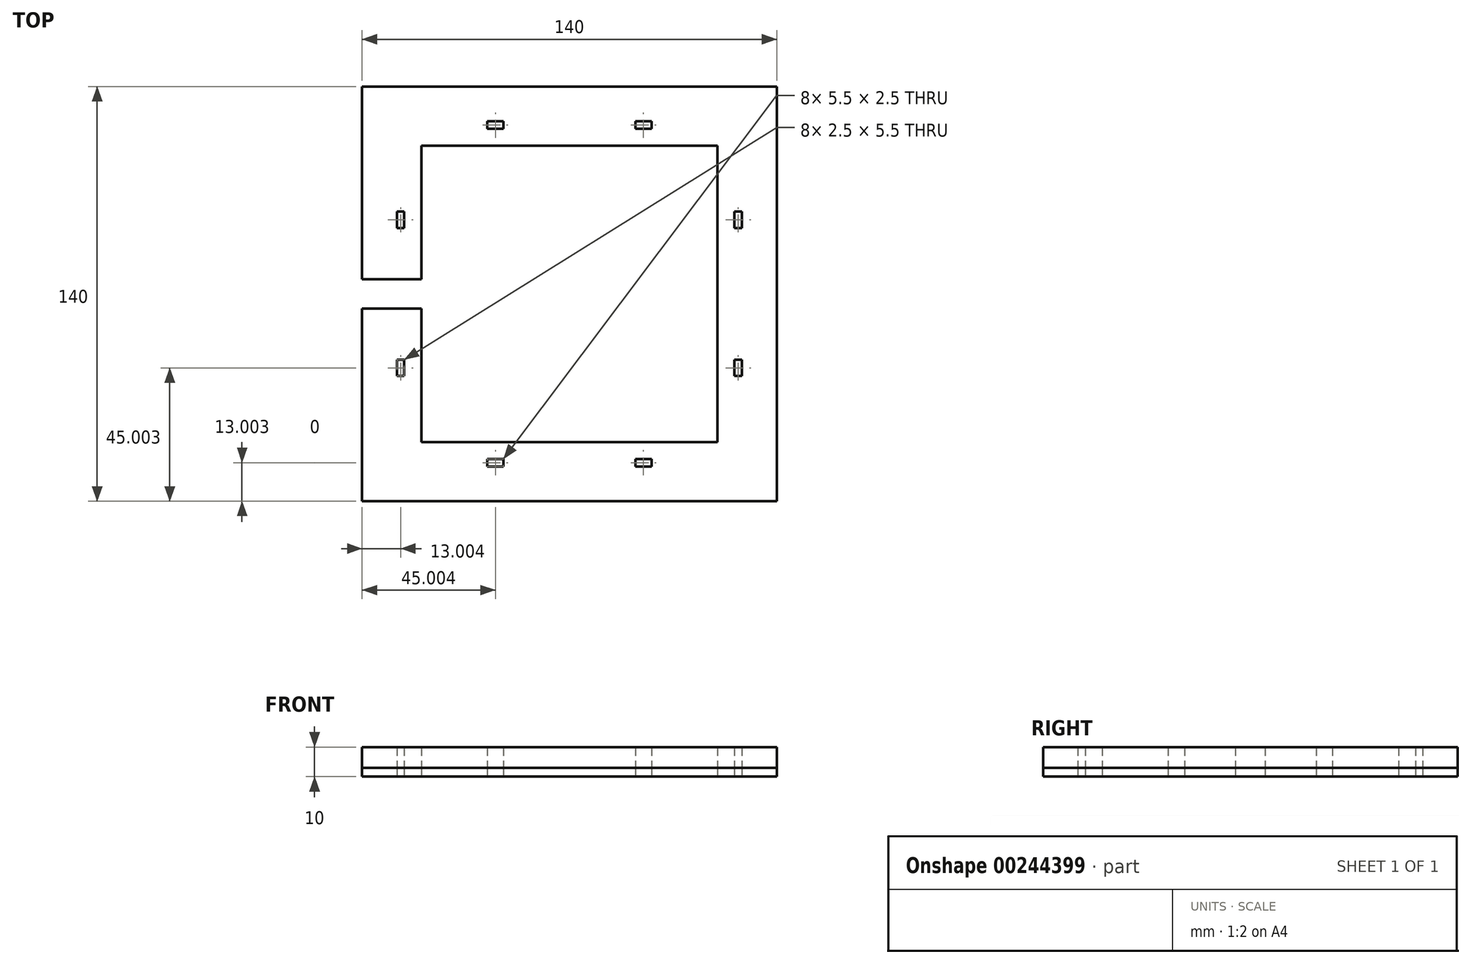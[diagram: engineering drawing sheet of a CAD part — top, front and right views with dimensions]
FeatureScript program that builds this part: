
annotation { "Feature Type Name" : "Feature", "Feature Type Description" : "" }
export const myFeature = defineFeature(function(context is Context, id is Id, definition is map)
    precondition{}
    {
        {
            var Q0;
            Q0=qCreatedBy(makeId("Top.planeOp"),FACE);
            var sketch = newSketch(context, id + "F0", { "sketchPlane" : qUnion([Q0])});
            skLineSegment(sketch, "E0.bottom", {"start": v(-61.18, 64.73) * mm, "end": v(38.82, 64.73) * mm});
            skLineSegment(sketch, "E0.top", {"start": v(-61.18, -35.27) * mm, "end": v(38.82, -35.27) * mm});
            skLineSegment(sketch, "E0.left", {"start": v(-61.18, 64.73) * mm, "end": v(-61.18, -35.27) * mm});
            skLineSegment(sketch, "E0.right", {"start": v(38.82, 64.73) * mm, "end": v(38.82, -35.27) * mm});
            skLineSegment(sketch, "E1.bottom", {"start": v(-81.18, 84.73) * mm, "end": v(58.82, 84.73) * mm});
            skLineSegment(sketch, "E1.top", {"start": v(-81.18, -55.27) * mm, "end": v(58.82, -55.27) * mm});
            skLineSegment(sketch, "E1.left", {"start": v(-81.18, 84.73) * mm, "end": v(-81.18, -55.27) * mm});
            skLineSegment(sketch, "E1.right", {"start": v(58.82, 84.73) * mm, "end": v(58.82, -55.27) * mm});
            skPoint(sketch, "E2", {"position": v(-11.18, 14.73) * mm});
            skLineSegment(sketch, "E3.bottom", {"start": v(53.82, -50.27) * mm, "end": v(-76.18, -50.27) * mm});
            skLineSegment(sketch, "E3.top", {"start": v(53.82, 79.73) * mm, "end": v(-76.18, 79.73) * mm});
            skLineSegment(sketch, "E3.left", {"start": v(53.82, -50.27) * mm, "end": v(53.82, 79.73) * mm});
            skLineSegment(sketch, "E3.right", {"start": v(-76.18, -50.27) * mm, "end": v(-76.18, 79.73) * mm});
            skLineSegment(sketch, "E4", {"start": v(-76.18, 71.73) * mm, "end": v(53.82, 71.73) * mm, "construction": true});
            skPoint(sketch, "E5", {"position": v(-36.18, 71.73) * mm});
            skPoint(sketch, "E6", {"position": v(13.82, 71.73) * mm});
            skLineSegment(sketch, "E7.bottom", {"start": v(-33.43, 70.48) * mm, "end": v(-38.93, 70.48) * mm});
            skLineSegment(sketch, "E7.top", {"start": v(-33.43, 72.98) * mm, "end": v(-38.93, 72.98) * mm});
            skLineSegment(sketch, "E7.left", {"start": v(-33.43, 70.48) * mm, "end": v(-33.43, 72.98) * mm});
            skLineSegment(sketch, "E7.right", {"start": v(-38.93, 70.48) * mm, "end": v(-38.93, 72.98) * mm});
            skPoint(sketch, "E8", {"position": v(-11.18, 71.73) * mm});
            skLineSegment(sketch, "E9", {"start": v(-11.18, 71.73) * mm, "end": v(-11.18, 68.28) * mm, "construction": true});
            skLineSegment(sketch, "E10.MirrorCS", {"start": v(11.07, 70.48) * mm, "end": v(11.07, 72.98) * mm});
            skLineSegment(sketch, "E11.MirrorCS", {"start": v(11.07, 72.98) * mm, "end": v(16.57, 72.98) * mm});
            skLineSegment(sketch, "E12.MirrorCS", {"start": v(16.57, 70.48) * mm, "end": v(16.57, 72.98) * mm});
            skLineSegment(sketch, "E13.MirrorCS", {"start": v(11.07, 70.48) * mm, "end": v(16.57, 70.48) * mm});
            skLineSegment(sketch, "E14.1.0", {"start": v(-69.43, -7.52) * mm, "end": v(-69.43, -13.02) * mm});
            skLineSegment(sketch, "E14.1.1", {"start": v(-66.93, -7.52) * mm, "end": v(-66.93, -13.02) * mm});
            skLineSegment(sketch, "E14.1.2", {"start": v(-66.93, -7.52) * mm, "end": v(-69.43, -7.52) * mm});
            skPoint(sketch, "E14.1.3", {"position": v(-68.18, -10.27) * mm});
            skLineSegment(sketch, "E14.1.4", {"start": v(-66.93, -13.02) * mm, "end": v(-69.43, -13.02) * mm});
            skPoint(sketch, "E14.1.5", {"position": v(-68.18, -10.27) * mm});
            skLineSegment(sketch, "E14.1.6", {"start": v(-69.43, 36.98) * mm, "end": v(-69.43, 42.48) * mm});
            skLineSegment(sketch, "E14.1.7", {"start": v(-66.93, 36.98) * mm, "end": v(-66.93, 42.48) * mm});
            skLineSegment(sketch, "E14.1.8", {"start": v(-66.93, 42.48) * mm, "end": v(-69.43, 42.48) * mm});
            skLineSegment(sketch, "E14.1.9", {"start": v(-66.93, 36.98) * mm, "end": v(-69.43, 36.98) * mm});
            skPoint(sketch, "E14.1.10", {"position": v(-68.18, 39.73) * mm});
            skLineSegment(sketch, "E14.1.11", {"start": v(-66.93, 36.98) * mm, "end": v(-66.93, 42.48) * mm});
            skLineSegment(sketch, "E14.1.12", {"start": v(-69.43, 36.98) * mm, "end": v(-69.43, 42.48) * mm});
            skLineSegment(sketch, "E14.1.13", {"start": v(-66.93, 36.98) * mm, "end": v(-69.43, 36.98) * mm});
            skLineSegment(sketch, "E14.1.14", {"start": v(-66.93, 42.48) * mm, "end": v(-69.43, 42.48) * mm});
            skPoint(sketch, "E14.1.15", {"position": v(-68.18, 39.73) * mm});
            skPoint(sketch, "E14.1.16", {"position": v(-68.18, 39.73) * mm});
            skPoint(sketch, "E14.1.17", {"position": v(-68.18, 39.73) * mm});
            skPoint(sketch, "E14.1.18", {"position": v(-68.18, 39.73) * mm});
            skLineSegment(sketch, "E14.2.0", {"start": v(11.07, -43.52) * mm, "end": v(16.57, -43.52) * mm});
            skLineSegment(sketch, "E14.2.1", {"start": v(11.07, -41.02) * mm, "end": v(16.57, -41.02) * mm});
            skLineSegment(sketch, "E14.2.2", {"start": v(11.07, -41.02) * mm, "end": v(11.07, -43.52) * mm});
            skPoint(sketch, "E14.2.3", {"position": v(13.82, -42.27) * mm});
            skLineSegment(sketch, "E14.2.4", {"start": v(16.57, -41.02) * mm, "end": v(16.57, -43.52) * mm});
            skPoint(sketch, "E14.2.5", {"position": v(13.82, -42.27) * mm});
            skLineSegment(sketch, "E14.2.6", {"start": v(-33.43, -43.52) * mm, "end": v(-38.93, -43.52) * mm});
            skLineSegment(sketch, "E14.2.7", {"start": v(-33.43, -41.02) * mm, "end": v(-38.93, -41.02) * mm});
            skLineSegment(sketch, "E14.2.8", {"start": v(-38.93, -41.02) * mm, "end": v(-38.93, -43.52) * mm});
            skLineSegment(sketch, "E14.2.9", {"start": v(-33.43, -41.02) * mm, "end": v(-33.43, -43.52) * mm});
            skPoint(sketch, "E14.2.10", {"position": v(-36.18, -42.27) * mm});
            skLineSegment(sketch, "E14.2.11", {"start": v(-33.43, -41.02) * mm, "end": v(-38.93, -41.02) * mm});
            skLineSegment(sketch, "E14.2.12", {"start": v(-33.43, -43.52) * mm, "end": v(-38.93, -43.52) * mm});
            skLineSegment(sketch, "E14.2.13", {"start": v(-33.43, -41.02) * mm, "end": v(-33.43, -43.52) * mm});
            skLineSegment(sketch, "E14.2.14", {"start": v(-38.93, -41.02) * mm, "end": v(-38.93, -43.52) * mm});
            skPoint(sketch, "E14.2.15", {"position": v(-36.18, -42.27) * mm});
            skPoint(sketch, "E14.2.16", {"position": v(-36.18, -42.27) * mm});
            skPoint(sketch, "E14.2.17", {"position": v(-36.18, -42.27) * mm});
            skPoint(sketch, "E14.2.18", {"position": v(-36.18, -42.27) * mm});
            skLineSegment(sketch, "E14.3.0", {"start": v(47.07, 36.98) * mm, "end": v(47.07, 42.48) * mm});
            skLineSegment(sketch, "E14.3.1", {"start": v(44.57, 36.98) * mm, "end": v(44.57, 42.48) * mm});
            skLineSegment(sketch, "E14.3.2", {"start": v(44.57, 36.98) * mm, "end": v(47.07, 36.98) * mm});
            skPoint(sketch, "E14.3.3", {"position": v(45.82, 39.73) * mm});
            skLineSegment(sketch, "E14.3.4", {"start": v(44.57, 42.48) * mm, "end": v(47.07, 42.48) * mm});
            skPoint(sketch, "E14.3.5", {"position": v(45.82, 39.73) * mm});
            skLineSegment(sketch, "E14.3.6", {"start": v(47.07, -7.52) * mm, "end": v(47.07, -13.02) * mm});
            skLineSegment(sketch, "E14.3.7", {"start": v(44.57, -7.52) * mm, "end": v(44.57, -13.02) * mm});
            skLineSegment(sketch, "E14.3.8", {"start": v(44.57, -13.02) * mm, "end": v(47.07, -13.02) * mm});
            skLineSegment(sketch, "E14.3.9", {"start": v(44.57, -7.52) * mm, "end": v(47.07, -7.52) * mm});
            skPoint(sketch, "E14.3.10", {"position": v(45.82, -10.27) * mm});
            skLineSegment(sketch, "E14.3.11", {"start": v(44.57, -7.52) * mm, "end": v(44.57, -13.02) * mm});
            skLineSegment(sketch, "E14.3.12", {"start": v(47.07, -7.52) * mm, "end": v(47.07, -13.02) * mm});
            skLineSegment(sketch, "E14.3.13", {"start": v(44.57, -7.52) * mm, "end": v(47.07, -7.52) * mm});
            skLineSegment(sketch, "E14.3.14", {"start": v(44.57, -13.02) * mm, "end": v(47.07, -13.02) * mm});
            skPoint(sketch, "E14.3.15", {"position": v(45.82, -10.27) * mm});
            skPoint(sketch, "E14.3.16", {"position": v(45.82, -10.27) * mm});
            skPoint(sketch, "E14.3.17", {"position": v(45.82, -10.27) * mm});
            skPoint(sketch, "E14.3.18", {"position": v(45.82, -10.27) * mm});
            skLineSegment(sketch, "E15", {"start": v(58.82, 14.73) * mm, "end": v(-81.18, 14.73) * mm, "construction": true});
            skLineSegment(sketch, "E16.bottom", {"start": v(-81.18, 19.73) * mm, "end": v(-61.18, 19.73) * mm});
            skLineSegment(sketch, "E16.top", {"start": v(-81.18, 9.73) * mm, "end": v(-61.18, 9.73) * mm});
            skLineSegment(sketch, "E16.left", {"start": v(-81.18, 19.73) * mm, "end": v(-81.18, 9.73) * mm});
            skLineSegment(sketch, "E16.right", {"start": v(-61.18, 19.73) * mm, "end": v(-61.18, 9.73) * mm});
            skLineSegment(sketch, "E17", {"start": v(-65.7, 14.73) * mm, "end": v(-65.7, 19.73) * mm, "construction": true});
            skLineSegment(sketch, "E18", {"start": v(-65.7, 19.73) * mm, "end": v(-65.7, 14.73) * mm, "construction": true});
            skLineSegment(sketch, "E19", {"start": v(-65.7, 9.73) * mm, "end": v(-65.7, 14.73) * mm, "construction": true});
            skSolve(sketch);
        }
        {
            var Q0;
            {var subQ5=sQuery(id+"F0.wireOp",EDGE,"E0.bottom");Q0=makeQuery(id+"F0.imprint","IMPRINT",FACE,{"disambiguationData":[TD([[makeQuery(id+"F0.imprint","IMPRINT",EDGE,{"derivedFrom":subQ5}),1.0]])]});}
            var Q1;
            {var subQ10=sQuery(id+"F0.wireOp",EDGE,"E1.bottom");Q1=makeQuery(id+"F0.imprint","IMPRINT",FACE,{"disambiguationData":[TD([[makeQuery(id+"F0.imprint","IMPRINT",EDGE,{"derivedFrom":subQ10}),-1.0]])]});}
            var Q2;
            {var subQ5=sQuery(id+"F0.wireOp",EDGE,"E16.right");Q2=makeQuery(id+"F0.imprint","IMPRINT",FACE,{"disambiguationData":[TD([[makeQuery(id+"F0.imprint","IMPRINT",EDGE,{"derivedFrom":subQ5}),-1.0]])]});}
            var Q3;
            {var subQ5=sQuery(id+"F0.wireOp",EDGE,"E16.left");Q3=makeQuery(id+"F0.imprint","IMPRINT",FACE,{"disambiguationData":[TD([[makeQuery(id+"F0.imprint","IMPRINT",EDGE,{"derivedFrom":subQ5}),1.0]])]});}
            extrude(context, id + "F1", {"entities" : qUnion([Q0, Q1, Q2, Q3]), "depth" : 3 * mm});
        }
        {
            var Q0;
            {var subQ5=sQuery(id+"F0.wireOp",EDGE,"E0.bottom");Q0=makeQuery(id+"F0.imprint","IMPRINT",FACE,{"disambiguationData":[TD([[makeQuery(id+"F0.imprint","IMPRINT",EDGE,{"derivedFrom":subQ5}),1.0]])]});}
            var Q1;
            {var subQ10=sQuery(id+"F0.wireOp",EDGE,"E1.bottom");Q1=makeQuery(id+"F0.imprint","IMPRINT",FACE,{"disambiguationData":[TD([[makeQuery(id+"F0.imprint","IMPRINT",EDGE,{"derivedFrom":subQ10}),-1.0]])]});}
            extrude(context, id + "F2", {"entities" : qUnion([Q0, Q1]), "depth" : 10 * mm});
        }
    });
